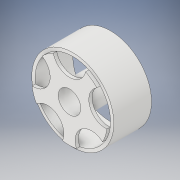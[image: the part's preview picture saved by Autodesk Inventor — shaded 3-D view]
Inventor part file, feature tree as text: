
AUTODESK INVENTOR PART (.ipt)
format: ipt  version: 2017 (Build 210142000, 142)  size: 164,864 bytes
history: native  units: in
note: dims shown in document units (in); Inventor stores cm internally (conversion verified against a paired STEP export)
features: extrude x3, sketch x3, projected_geometry x2, pattern_circular x1
ambient origin geometry x8: Origin, YZ Plane, XZ Plane, XY Plane, X Axis, Y Axis, Z Axis, Center Point
bodies: Solid1 (feature_tree)
feature tree (9):
  extrude  "Extrusion1"  Depth=0.05in
  sketch  "Sketch2"  dims[d2=0.35in d3=0.05in]
  extrude  "Extrusion2"  Depth=0.05in
  extrude  "Extrusion3"  Depth=0.05in TaperAngle=0.0deg
  pattern_circular  "Circular Pattern1"  [2 undecoded]
  sketch  "Sketch1"  dims[d0=0.44in d1=0.05in]
  projected_geometry  "Projected Loop1"
  projected_geometry  "Projected Loop2"
  sketch  "Sketch4"  dims[d4=0.57in d5=0.0in d6=0.05in d7=0.0in d8=0.5in d9=1.9685in d11=360.0deg d13=0.25in d14=0.25in d15=1.14in d16=0.15in d17=0.34in d18=0.05in d19=0.0in d20=1.9685in d21=360.0deg]
note: 2 required parameter values undecoded (feature->parameter linkage not recoverable at this tier; creation-order binding heuristic only, values carry confidence <= 0.55)
